# Revit family: UNB_Adapto_U8425_BIM_DE
name_source: partatom
category: Plumbing Fixtures
revit_build: Autodesk Revit 2017 (Build: 20160225_1515(x64)
units: mm (PartAtom-declared; Revit-internal decimal feet)

## family parameters
Always vertical = No
Cut with Voids When Loaded = No
OmniClass Number = 23.45.05.14.21.11
OmniClass Title = Bath/Shower Units
Part Type = Normal
Room Calculation Point = No
Round Connector Dimension = Use Diameter
Shared = No
Work Plane-Based = No

## types (1)
- U8425AA - ADAPTO TW/RAIL CHROME SNOOPY
    Accessories = http://www.idealstandard.de
    AreaUnits = Millimeter
    AssetType = Fest
    BIMObjectName = ISI_IdealStandard_BathroomFurniture_Adapto_U8425AA
    BIMobject category = Accessories
    BIMobject category code = sanitary-accessories1
    BIMobject main category = Sanitary
    BIMobject main category code = sanitary
    BOSUseNativeGeometries = 1
    Brand = Ideal Standard
    Brand url = http://www.idealstandard.co.uk
    CodePerformance = FSC
    Color = Chrome
    ConnectionType = Mechanical
    Cost = 0 $
    CurrencyUnit = €
    CurrentRevision = 1
    Date of publishing = 2018_04_13
    Description = ADAPTO TW/RAIL CHROME SNOOPY
    DurationUnit = Jahr
    Edition number = 1
    Features = TW/RAIL CHROME SNOOPY
    Finish = Chrome
    IfcExportAs = IfcFurnitureType
    IfcExportType = BATHROOM FURNITURE
    Installation instructions = http://www.idealstandard.de
    InstallationDate = 1900-12-31T23:59:59
    InstallationInstructions = http://www.idealstandard.de
    LinearUnits = Millimeter
    MainColor = Chrome
    MaintenanceInformation = http://www.idealstandard.de
    Manufacturer name = Ideal Standard
    ManufacturerURL = http://www.idealstandard.de
    Model = U8425AA
    ModelNumber = U8425AA
    ModelReference = ADAPTO TW/RAIL CHROME SNOOPY
    NBS Reference Code = 45-35-72/320
    NBS Reference Description = Bathroom Integrated Ductwork
    Name = IdealStandard_BathroomFurniture_Adapto_U8425AA_ISI
    NettWeight = 0,50 KG
    Nominal height = 35
    Nominal width = 360
    NominalDepth = 20 mm  [stored 0.0656168 ft]
    NominalHeight = 35 mm  [stored 0.114829 ft]
    NominalLength = 20 mm  [stored 0.0656168 ft]
    NominalWidth = 360 mm  [stored 1.1811 ft]
    Product Guid = 14b4b9d1-9558-4d6d-bcd9-fec63e520bba
    Product SKU = U8425
    Product data url = https://bimobject.com
    Product family = Sanitary
    Product group = Bathroom Furniture
    Product name = ADAPTO TW/RAIL CHROME SNOOPY
    Product url = http://www.idealstandard.de
    ProductInformation = http://www.idealstandard.de
    QR code = http://bimobject.com
    ReplacementCost = 0
    Shape = Rechteckig
    Size = 35 x20 x 360mm
    Space = intern
    SpareParts = http://www.idealstandard.de
    SustainabilityPerformance = FSC
    Technical description = http://www.idealstandard.de
    URL = http://www.idealstandard.de
    Uniclass 2.0 Code = Pr_40_30_78_05
    Uniclass 2.0 Description = Bathroom furniture
    Uniclass 2015 Code = Pr_40_30_78_05
    Uniclass 2015 Name = Bathroom furniture
    Uniclass2015Code = Pr_40_30_78_05
    Uniclass2015Title = Bathroom furniture
    Uniclass2015Version = Products v1.1
    Version = 1
    VolumeUnits = Litres
    WarrantyStartDate = 1900-12-31T23:59:59
    Weight Net (Kg) = 0

note: [stored X ft] marks values corroborated as IEEE doubles in the binary element streams (Revit-internal decimal feet)

## geometry (parser evidence)
native form markers: Sweep x2
no freeform markers — native parametric forms only
